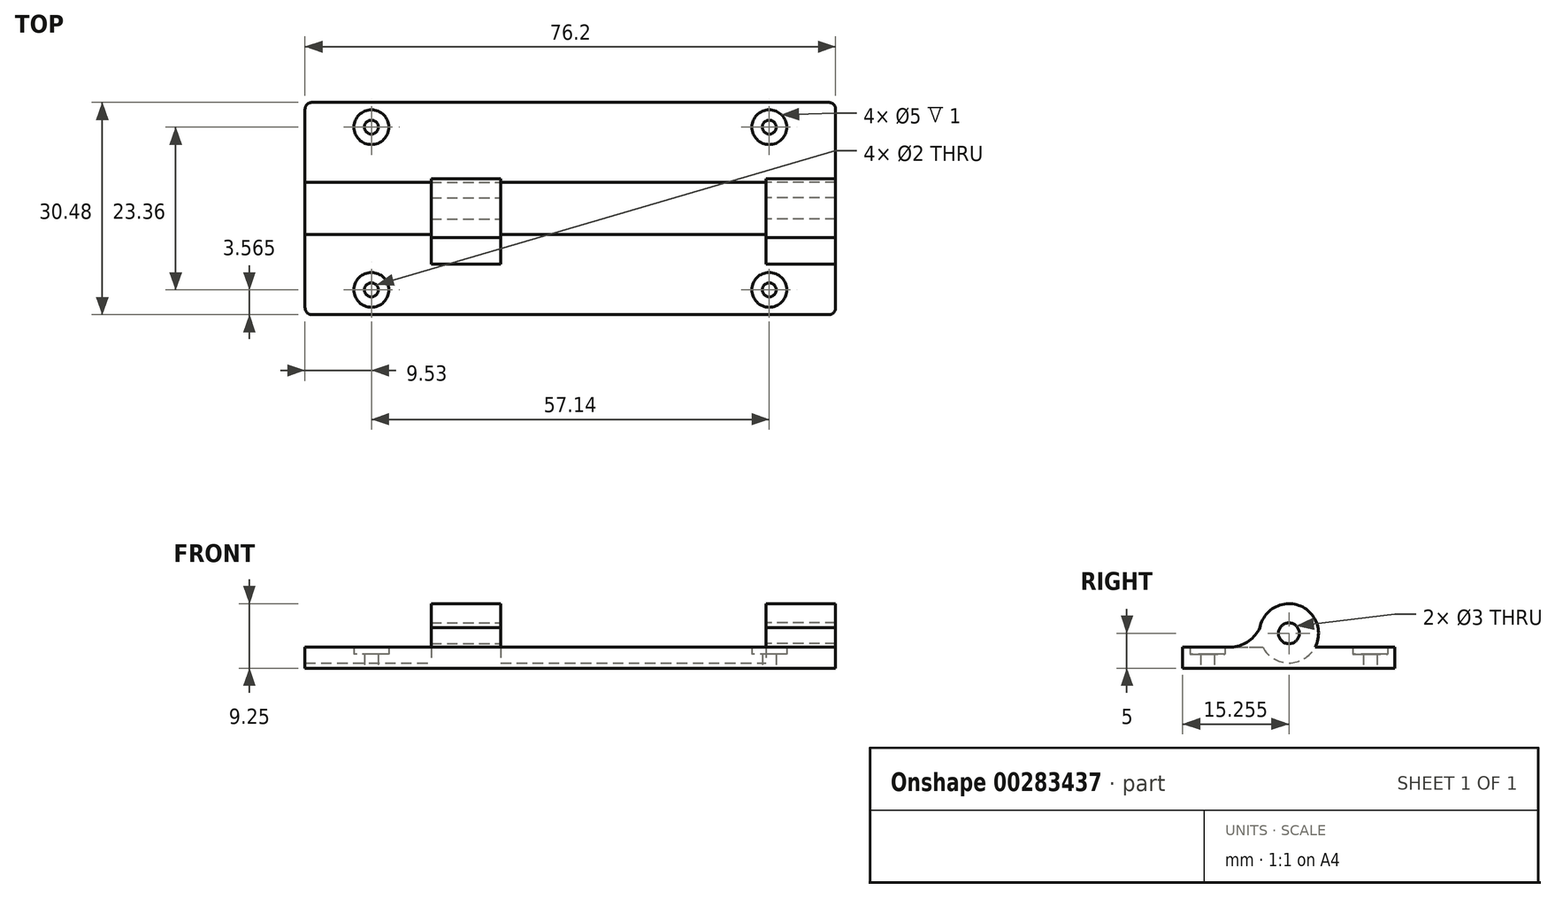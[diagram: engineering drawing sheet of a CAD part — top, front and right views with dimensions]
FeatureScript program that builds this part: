
annotation { "Feature Type Name" : "Feature", "Feature Type Description" : "" }
export const myFeature = defineFeature(function(context is Context, id is Id, definition is map)
    precondition{}
    {
        {
            var Q0;
            Q0=qCreatedBy(makeId("Top.planeOp"),FACE);
            var sketch = newSketch(context, id + "F0", { "sketchPlane" : qUnion([Q0])});
            skLineSegment(sketch, "E0.bottom", {"start": v(-38.1, -13.62) * mm, "end": v(38.1, -13.62) * mm});
            skLineSegment(sketch, "E0.top", {"start": v(-38.1, 16.86) * mm, "end": v(38.1, 16.86) * mm});
            skLineSegment(sketch, "E0.left", {"start": v(-38.1, -13.62) * mm, "end": v(-38.1, 16.86) * mm});
            skLineSegment(sketch, "E0.right", {"start": v(38.1, -13.62) * mm, "end": v(38.1, 16.86) * mm});
            skCircle(sketch, "E1", {"center": v(-28.57, -10.06) * mm, "radius": 1 * mm});
            skCircle(sketch, "E2", {"center": v(28.57, -10.06) * mm, "radius": 1 * mm});
            skCircle(sketch, "E3", {"center": v(28.57, 13.3) * mm, "radius": 1 * mm});
            skCircle(sketch, "E4", {"center": v(-28.57, 13.3) * mm, "radius": 1 * mm});
            skCircle(sketch, "E5", {"center": v(-28.57, 13.3) * mm, "radius": 2.5 * mm});
            skCircle(sketch, "E6", {"center": v(28.57, 13.3) * mm, "radius": 2.5 * mm});
            skCircle(sketch, "E7", {"center": v(28.57, -10.06) * mm, "radius": 2.5 * mm});
            skCircle(sketch, "E8", {"center": v(-28.57, -10.06) * mm, "radius": 2.5 * mm});
            skSolve(sketch);
        }
        {
            var Q0;
            Q0=qCreatedBy(makeId("Right.planeOp"),FACE);
            var sketch = newSketch(context, id + "F1", { "sketchPlane" : qUnion([Q0])});
            skLineSegment(sketch, "E9.bottom", {"start": v(-13.62, 0) * mm, "end": v(16.86, 0) * mm});
            skLineSegment(sketch, "E9.top", {"start": v(-13.62, 3) * mm, "end": v(16.86, 3) * mm});
            skLineSegment(sketch, "E9.left", {"start": v(-13.62, 0) * mm, "end": v(-13.62, 3) * mm});
            skLineSegment(sketch, "E9.right", {"start": v(16.86, 0) * mm, "end": v(16.86, 3) * mm});
            skCircle(sketch, "E10", {"center": v(1.63, 5) * mm, "radius": 4.25 * mm});
            skLineSegment(sketch, "E11", {"start": v(-6.37, 3) * mm, "end": v(-6.37, 5) * mm});
            skArc(sketch, "E12", {"start": v(-6.37, 3) * mm, "mid": v(-4.1, 3.92) * mm, "end": v(-2.54, 5.8) * mm});
            skLineSegment(sketch, "E13", {"start": v(1.63, 5) * mm, "end": v(1.63, 4) * mm});
            skArc(sketch, "E14.MirrorCS", {"start": v(9.63, 3) * mm, "mid": v(7.37, 3.92) * mm, "end": v(5.8, 5.8) * mm});
            skCircle(sketch, "E15", {"center": v(1.63, 5) * mm, "radius": 1.5 * mm});
            skSolve(sketch);
        }
        {
            var Q0;
            Q0=makeQuery(id+"F0.imprint","IMPRINT",FACE,{"disambiguationData":[TD([[makeQuery(id+"F0.imprint","IMPRINT",EDGE,{"derivedFrom":sQuery(id+"F0.wireOp",EDGE,"E0.bottom")}),1.0]])]});
            extrude(context, id + "F2", {"entities" : qUnion([Q0]), "depth" : 3 * mm, "offsetDistance" : 25 * mm});
        }
        {
            var Q0;
            Q0=makeQuery(id+"F0.imprint","IMPRINT",FACE,{"disambiguationData":[TD([[makeQuery(id+"F0.imprint","IMPRINT",EDGE,{"derivedFrom":sQuery(id+"F0.wireOp",EDGE,"E3")}),-1.0]])]});
            var Q1;
            Q1=makeQuery(id+"F0.imprint","IMPRINT",FACE,{"disambiguationData":[TD([[makeQuery(id+"F0.imprint","IMPRINT",EDGE,{"derivedFrom":sQuery(id+"F0.wireOp",EDGE,"E2")}),-1.0]])]});
            var Q2;
            Q2=makeQuery(id+"F0.imprint","IMPRINT",FACE,{"disambiguationData":[TD([[makeQuery(id+"F0.imprint","IMPRINT",EDGE,{"derivedFrom":sQuery(id+"F0.wireOp",EDGE,"E1")}),-1.0]])]});
            var Q3;
            Q3=makeQuery(id+"F0.imprint","IMPRINT",FACE,{"disambiguationData":[TD([[makeQuery(id+"F0.imprint","IMPRINT",EDGE,{"derivedFrom":sQuery(id+"F0.wireOp",EDGE,"E4")}),-1.0]])]});
            extrude(context, id + "F3", {"entities" : qUnion([Q0, Q1, Q2, Q3]), "operationType" : NewBodyOperationType.ADD, "depth" : 2 * mm, "offsetDistance" : 25 * mm});
        }
        {
            var Q0;
            {var subQ0=sQuery(id+"F1.wireOp",EDGE,"E14.MirrorCS");Q0=makeQuery(id+"F1.imprint","IMPRINT",FACE,{"disambiguationData":[TD([[makeQuery(id+"F1.imprint","IMPRINT",EDGE,{"derivedFrom":subQ0}),1.0]])]});}
            var Q1;
            {var subQ7=sQuery(id+"F1.wireOp",EDGE,"E15");var subQ8=makeQuery(id+"F1.imprint","IMPRINT",VERTEX,{"disambiguationData":[OD(0.0)],"derivedFrom":subQ7});Q1=makeQuery(id+"F1.imprint","IMPRINT",FACE,{"disambiguationData":[TD([[makeQuery(id+"F1.imprint","IMPRINT",EDGE,{"disambiguationData":[TD([[subQ8,-1.0]])],"derivedFrom":subQ7}),-1.0]])]});}
            var Q2;
            {var subQ3=sQuery(id+"F1.wireOp",EDGE,"E12");Q2=makeQuery(id+"F1.imprint","IMPRINT",FACE,{"disambiguationData":[TD([[makeQuery(id+"F1.imprint","IMPRINT",EDGE,{"derivedFrom":subQ3}),-1.0]])]});}
            extrude(context, id + "F4", {"entities" : qUnion([Q0, Q1, Q2]), "operationType" : NewBodyOperationType.ADD, "depth" : 38.1 * mm, "offsetDistance" : 25 * mm, "hasSecondDirection" : true, "secondDirectionOppositeDirection" : false, "secondDirectionDepth" : 28.1 * mm});
        }
        {
            var Q0;
            {var subQ0=sQuery(id+"F1.wireOp",EDGE,"E14.MirrorCS");Q0=makeQuery(id+"F1.imprint","IMPRINT",FACE,{"disambiguationData":[TD([[makeQuery(id+"F1.imprint","IMPRINT",EDGE,{"derivedFrom":subQ0}),1.0]])]});}
            var Q1;
            {var subQ7=sQuery(id+"F1.wireOp",EDGE,"E15");var subQ8=makeQuery(id+"F1.imprint","IMPRINT",VERTEX,{"disambiguationData":[OD(0.0)],"derivedFrom":subQ7});Q1=makeQuery(id+"F1.imprint","IMPRINT",FACE,{"disambiguationData":[TD([[makeQuery(id+"F1.imprint","IMPRINT",EDGE,{"disambiguationData":[TD([[subQ8,-1.0]])],"derivedFrom":subQ7}),-1.0]])]});}
            var Q2;
            {var subQ3=sQuery(id+"F1.wireOp",EDGE,"E12");Q2=makeQuery(id+"F1.imprint","IMPRINT",FACE,{"disambiguationData":[TD([[makeQuery(id+"F1.imprint","IMPRINT",EDGE,{"derivedFrom":subQ3}),-1.0]])]});}
            extrude(context, id + "F5", {"entities" : qUnion([Q0, Q1, Q2]), "operationType" : NewBodyOperationType.ADD, "oppositeDirection" : true, "depth" : 20 * mm, "offsetDistance" : 25 * mm, "hasSecondDirection" : true, "secondDirectionOppositeDirection" : true, "secondDirectionDepth" : 10 * mm});
        }
        {
            var Q0;
            {var subQ0=sQuery(id+"F1.wireOp",EDGE,"E10");var subQ1=sQuery(id+"F1.wireOp",EDGE,"E9.top");var subQ2=makeQuery(id+"F1.imprint","INTERSECT",VERTEX,{"disambiguationData":[OD(0.0)],"derivedFrom":[subQ1,subQ0]});Q0=makeQuery(id+"F1.imprint","IMPRINT",FACE,{"disambiguationData":[TD([[makeQuery(id+"F1.imprint","IMPRINT",EDGE,{"disambiguationData":[TD([[subQ2,-1.0]])],"derivedFrom":subQ1}),-1.0]])]});}
            extrude(context, id + "F6", {"entities" : qUnion([Q0]), "operationType" : NewBodyOperationType.REMOVE, "oppositeDirection" : true, "depth" : 10 * mm, "offsetDistance" : 25 * mm, "hasSecondDirection" : true, "secondDirectionOppositeDirection" : false, "secondDirectionDepth" : 28.1 * mm});
        }
        {
            var Q0;
            Q0=makeQuery(id+"F2.opExtrude","SWEPT_EDGE",EDGE,{"disambiguationData":[OSD([sQuery(id+"F0.wireOp",EDGE,"E0.bottom"),sQuery(id+"F0.wireOp",EDGE,"E0.right")])]});
            var Q1;
            Q1=makeQuery(id+"F2.opExtrude","SWEPT_EDGE",EDGE,{"disambiguationData":[OSD([sQuery(id+"F0.wireOp",EDGE,"E0.top"),sQuery(id+"F0.wireOp",EDGE,"E0.right")])]});
            var Q2;
            Q2=makeQuery(id+"F2.opExtrude","SWEPT_EDGE",EDGE,{"disambiguationData":[OSD([sQuery(id+"F0.wireOp",EDGE,"E0.top"),sQuery(id+"F0.wireOp",EDGE,"E0.left")])]});
            var Q3;
            Q3=makeQuery(id+"F2.opExtrude","SWEPT_EDGE",EDGE,{"disambiguationData":[OSD([sQuery(id+"F0.wireOp",EDGE,"E0.bottom"),sQuery(id+"F0.wireOp",EDGE,"E0.left")])]});
            fillet(context, id + "F7", {"entities" : qUnion([Q0, Q1, Q2, Q3]), "tangentPropagation" : true, "radius" : 1 * mm, "defaultsChanged" : false, "vertexSettings" : [], "allowEdgeOverflow" : false});
        }
        {
            var Q0;
            Q0=makeQuery(id+"F1.imprint","IMPRINT",FACE,{"disambiguationData":[TD([[makeQuery(id+"F1.imprint","IMPRINT",EDGE,{"derivedFrom":sQuery(id+"F1.wireOp",EDGE,"E15")}),-1.0]])]});
            var Q1;
            {var subQ0=sQuery(id+"F1.wireOp",EDGE,"E10");var subQ1=sQuery(id+"F1.wireOp",EDGE,"E9.top");var subQ2=makeQuery(id+"F1.imprint","INTERSECT",VERTEX,{"disambiguationData":[OD(0.0)],"derivedFrom":[subQ1,subQ0]});Q1=makeQuery(id+"F1.imprint","IMPRINT",FACE,{"disambiguationData":[TD([[makeQuery(id+"F1.imprint","IMPRINT",EDGE,{"disambiguationData":[TD([[subQ2,-1.0]])],"derivedFrom":subQ1}),-1.0]])]});}
            extrude(context, id + "F8", {"entities" : qUnion([Q0, Q1]), "operationType" : NewBodyOperationType.REMOVE, "oppositeDirection" : true, "depth" : 50 * mm, "offsetDistance" : 25 * mm, "hasSecondDirection" : true, "secondDirectionOppositeDirection" : true, "secondDirectionDepth" : 20 * mm});
        }
    });
